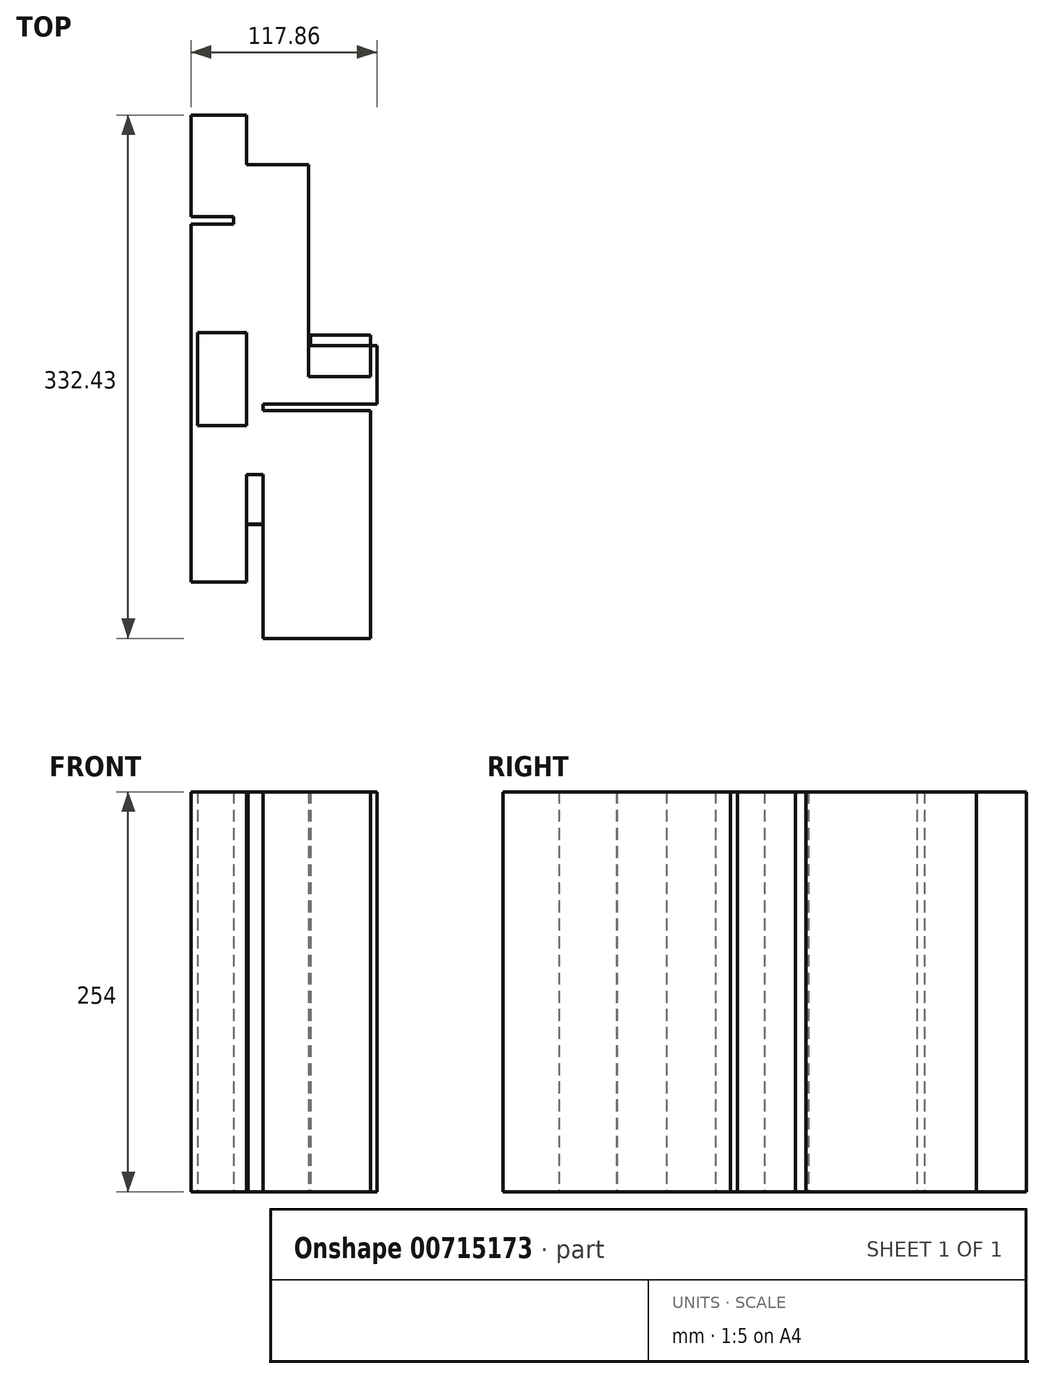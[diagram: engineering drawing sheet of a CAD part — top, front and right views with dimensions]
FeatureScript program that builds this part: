
annotation { "Feature Type Name" : "Feature", "Feature Type Description" : "" }
export const myFeature = defineFeature(function(context is Context, id is Id, definition is map)
    precondition{}
    {
        {
            var Q0;
            Q0=qCreatedBy(makeId("Top.planeOp"),FACE);
            var sketch = newSketch(context, id + "F0", { "sketchPlane" : qUnion([Q0])});
            skLineSegment(sketch, "E0.bottom", {"start": v(-63.35, 222.38) * mm, "end": v(-28.3, 222.38) * mm});
            skLineSegment(sketch, "E0.top", {"start": v(-63.35, 190.91) * mm, "end": v(-28.3, 190.91) * mm});
            skLineSegment(sketch, "E0.left", {"start": v(-63.35, 222.38) * mm, "end": v(-63.35, 190.91) * mm});
            skLineSegment(sketch, "E0.right", {"start": v(-28.3, 222.38) * mm, "end": v(-28.3, 190.91) * mm});
            skLineSegment(sketch, "E1.bottom", {"start": v(-28.3, 190.91) * mm, "end": v(11.26, 190.91) * mm});
            skLineSegment(sketch, "E1.top", {"start": v(-28.3, 157.75) * mm, "end": v(11.26, 157.75) * mm});
            skLineSegment(sketch, "E1.left", {"start": v(-28.3, 190.91) * mm, "end": v(-28.3, 157.75) * mm});
            skLineSegment(sketch, "E1.right", {"start": v(11.26, 190.91) * mm, "end": v(11.26, 157.75) * mm});
            skLineSegment(sketch, "E2.bottom", {"start": v(-28.3, 157.75) * mm, "end": v(-36.35, 157.75) * mm});
            skLineSegment(sketch, "E2.top", {"start": v(-28.3, 84) * mm, "end": v(-36.35, 84) * mm});
            skLineSegment(sketch, "E2.left", {"start": v(-28.3, 157.75) * mm, "end": v(-28.3, 84) * mm});
            skLineSegment(sketch, "E2.right", {"start": v(-36.35, 157.75) * mm, "end": v(-36.35, 84) * mm});
            skLineSegment(sketch, "E3.bottom", {"start": v(-28.3, 84) * mm, "end": v(11.26, 84) * mm});
            skLineSegment(sketch, "E3.left", {"start": v(-28.3, 84) * mm, "end": v(-28.3, 157.75) * mm});
            skLineSegment(sketch, "E3.right", {"start": v(11.26, 84) * mm, "end": v(11.26, 157.75) * mm});
            skLineSegment(sketch, "E4.bottom", {"start": v(-63.35, 190.91) * mm, "end": v(-32.32, 190.91) * mm});
            skLineSegment(sketch, "E4.top", {"start": v(-63.35, 157.75) * mm, "end": v(-32.32, 157.75) * mm});
            skLineSegment(sketch, "E4.left", {"start": v(-63.35, 190.91) * mm, "end": v(-63.35, 157.75) * mm});
            skLineSegment(sketch, "E4.right", {"start": v(-32.32, 190.91) * mm, "end": v(-32.32, 157.75) * mm});
            skLineSegment(sketch, "E5.bottom", {"start": v(-63.35, 152.88) * mm, "end": v(-36.35, 152.88) * mm});
            skLineSegment(sketch, "E5.top", {"start": v(-63.35, 120.88) * mm, "end": v(-36.35, 120.88) * mm});
            skLineSegment(sketch, "E5.left", {"start": v(-63.35, 152.88) * mm, "end": v(-63.35, 120.88) * mm});
            skLineSegment(sketch, "E5.right", {"start": v(-36.35, 152.88) * mm, "end": v(-36.35, 120.88) * mm});
            skLineSegment(sketch, "E6.top", {"start": v(-63.35, 84) * mm, "end": v(-36.35, 84) * mm});
            skLineSegment(sketch, "E6.left", {"start": v(-63.35, 120.88) * mm, "end": v(-63.35, 84) * mm});
            skLineSegment(sketch, "E6.right", {"start": v(-36.35, 120.88) * mm, "end": v(-36.35, 84) * mm});
            skLineSegment(sketch, "E7.bottom", {"start": v(-35.17, 82.33) * mm, "end": v(-63.35, 82.33) * mm});
            skLineSegment(sketch, "E7.top", {"start": v(-35.17, 84) * mm, "end": v(-63.35, 84) * mm});
            skLineSegment(sketch, "E7.left", {"start": v(-35.17, 82.33) * mm, "end": v(-35.17, 84) * mm});
            skLineSegment(sketch, "E7.right", {"start": v(-63.35, 82.33) * mm, "end": v(-63.35, 84) * mm});
            skLineSegment(sketch, "E8.bottom", {"start": v(-59.48, 84) * mm, "end": v(-28.3, 84) * mm});
            skLineSegment(sketch, "E8.top", {"start": v(-59.48, 56.06) * mm, "end": v(-28.3, 56.06) * mm});
            skLineSegment(sketch, "E8.left", {"start": v(-59.48, 84) * mm, "end": v(-59.48, 56.06) * mm});
            skLineSegment(sketch, "E8.right", {"start": v(-28.3, 84) * mm, "end": v(-28.3, 56.06) * mm});
            skLineSegment(sketch, "E9.bottom", {"start": v(-30.15, 56.06) * mm, "end": v(11.26, 56.06) * mm});
            skLineSegment(sketch, "E9.top", {"start": v(-30.15, 84) * mm, "end": v(11.26, 84) * mm});
            skLineSegment(sketch, "E9.left", {"start": v(-30.15, 56.06) * mm, "end": v(-30.15, 84) * mm});
            skLineSegment(sketch, "E9.right", {"start": v(11.26, 56.06) * mm, "end": v(11.26, 84) * mm});
            skLineSegment(sketch, "E10.bottom", {"start": v(12.56, 82.64) * mm, "end": v(50.4, 82.64) * mm});
            skLineSegment(sketch, "E10.top", {"start": v(12.56, 75.72) * mm, "end": v(50.4, 75.72) * mm});
            skLineSegment(sketch, "E10.left", {"start": v(12.56, 82.64) * mm, "end": v(12.56, 75.72) * mm});
            skLineSegment(sketch, "E10.right", {"start": v(50.4, 82.64) * mm, "end": v(50.4, 75.72) * mm});
            skLineSegment(sketch, "E11.bottom", {"start": v(50.4, 75.72) * mm, "end": v(54.51, 75.72) * mm});
            skLineSegment(sketch, "E11.top", {"start": v(50.4, 38.84) * mm, "end": v(54.51, 38.84) * mm});
            skLineSegment(sketch, "E11.left", {"start": v(50.4, 75.72) * mm, "end": v(50.4, 38.84) * mm});
            skLineSegment(sketch, "E11.right", {"start": v(54.51, 75.72) * mm, "end": v(54.51, 38.84) * mm});
            skLineSegment(sketch, "E12.bottom", {"start": v(50.4, 38.84) * mm, "end": v(15.56, 38.84) * mm});
            skLineSegment(sketch, "E12.top", {"start": v(50.4, 56.06) * mm, "end": v(15.56, 56.06) * mm});
            skLineSegment(sketch, "E12.left", {"start": v(50.4, 38.84) * mm, "end": v(50.4, 56.06) * mm});
            skLineSegment(sketch, "E12.right", {"start": v(15.56, 38.84) * mm, "end": v(15.56, 56.06) * mm});
            skLineSegment(sketch, "E13.bottom", {"start": v(15.56, 56.06) * mm, "end": v(-17.63, 56.06) * mm});
            skLineSegment(sketch, "E13.top", {"start": v(15.56, 38.84) * mm, "end": v(-17.63, 38.84) * mm});
            skLineSegment(sketch, "E13.left", {"start": v(15.56, 56.06) * mm, "end": v(15.56, 38.84) * mm});
            skLineSegment(sketch, "E13.right", {"start": v(-17.63, 56.06) * mm, "end": v(-17.63, 38.84) * mm});
            skLineSegment(sketch, "E14.bottom", {"start": v(-17.63, 38.84) * mm, "end": v(-48.59, 38.84) * mm});
            skLineSegment(sketch, "E14.top", {"start": v(-17.63, 24.9) * mm, "end": v(-48.59, 24.9) * mm});
            skLineSegment(sketch, "E14.left", {"start": v(-17.63, 38.84) * mm, "end": v(-17.63, 24.9) * mm});
            skLineSegment(sketch, "E14.right", {"start": v(-48.59, 38.84) * mm, "end": v(-48.59, 24.9) * mm});
            skLineSegment(sketch, "E15.bottom", {"start": v(-48.59, 24.9) * mm, "end": v(-59.48, 24.9) * mm});
            skLineSegment(sketch, "E15.top", {"start": v(-48.59, 56.06) * mm, "end": v(-59.48, 56.06) * mm});
            skLineSegment(sketch, "E15.left", {"start": v(-48.59, 24.9) * mm, "end": v(-48.59, 56.06) * mm});
            skLineSegment(sketch, "E15.right", {"start": v(-59.48, 24.9) * mm, "end": v(-59.48, 56.06) * mm});
            skLineSegment(sketch, "E16.bottom", {"start": v(-28.3, -74.3) * mm, "end": v(-63.35, -74.3) * mm});
            skLineSegment(sketch, "E16.top", {"start": v(-28.3, 82.33) * mm, "end": v(-63.35, 82.33) * mm});
            skLineSegment(sketch, "E16.left", {"start": v(-28.3, -74.3) * mm, "end": v(-28.3, 82.33) * mm});
            skLineSegment(sketch, "E16.right", {"start": v(-63.35, -74.3) * mm, "end": v(-63.35, 82.33) * mm});
            skLineSegment(sketch, "E17.bottom", {"start": v(-17.63, -110.05) * mm, "end": v(50.4, -110.05) * mm});
            skLineSegment(sketch, "E17.top", {"start": v(-17.63, 34.58) * mm, "end": v(50.4, 34.58) * mm});
            skLineSegment(sketch, "E17.left", {"start": v(-17.63, -110.05) * mm, "end": v(-17.63, 34.58) * mm});
            skLineSegment(sketch, "E17.right", {"start": v(50.4, -110.05) * mm, "end": v(50.4, 34.58) * mm});
            skLineSegment(sketch, "E18.bottom", {"start": v(-17.63, 24.9) * mm, "end": v(-17.63, 24.9) * mm});
            skLineSegment(sketch, "E18.top", {"start": v(-17.63, -5.97) * mm, "end": v(-17.63, -5.97) * mm});
            skLineSegment(sketch, "E18.left", {"start": v(-17.63, 24.9) * mm, "end": v(-17.63, -5.97) * mm});
            skLineSegment(sketch, "E18.right", {"start": v(-17.63, 24.9) * mm, "end": v(-17.63, -5.97) * mm});
            skLineSegment(sketch, "E19.bottom", {"start": v(-15.97, -5.97) * mm, "end": v(-28.3, -5.97) * mm});
            skLineSegment(sketch, "E19.top", {"start": v(-15.97, -5.97) * mm, "end": v(-28.3, -5.97) * mm});
            skLineSegment(sketch, "E19.left", {"start": v(-15.97, -5.97) * mm, "end": v(-15.97, -5.97) * mm});
            skLineSegment(sketch, "E19.right", {"start": v(-28.3, -5.97) * mm, "end": v(-28.3, -5.97) * mm});
            skLineSegment(sketch, "E20.bottom", {"start": v(-29.05, -7.22) * mm, "end": v(-28.3, -7.22) * mm});
            skLineSegment(sketch, "E20.top", {"start": v(-29.05, -37.56) * mm, "end": v(-28.3, -37.56) * mm});
            skLineSegment(sketch, "E20.left", {"start": v(-29.05, -7.22) * mm, "end": v(-29.05, -37.56) * mm});
            skLineSegment(sketch, "E20.right", {"start": v(-28.3, -7.22) * mm, "end": v(-28.3, -37.56) * mm});
            skLineSegment(sketch, "E21.bottom", {"start": v(-27.25, -37.56) * mm, "end": v(-17.63, -37.56) * mm});
            skLineSegment(sketch, "E21.top", {"start": v(-27.25, -37.74) * mm, "end": v(-17.63, -37.74) * mm});
            skLineSegment(sketch, "E21.left", {"start": v(-27.25, -37.56) * mm, "end": v(-27.25, -37.74) * mm});
            skLineSegment(sketch, "E21.right", {"start": v(-17.63, -37.56) * mm, "end": v(-17.63, -37.74) * mm});
            skSolve(sketch);
        }
        {
            var Q0;
            Q0 = qSketchRegion(id + "F0", true);
            extrude(context, id + "F1", {"entities" : qUnion([Q0]), "depth" : 254 * mm, "offsetDistance" : 25.4 * mm});
        }
    });
